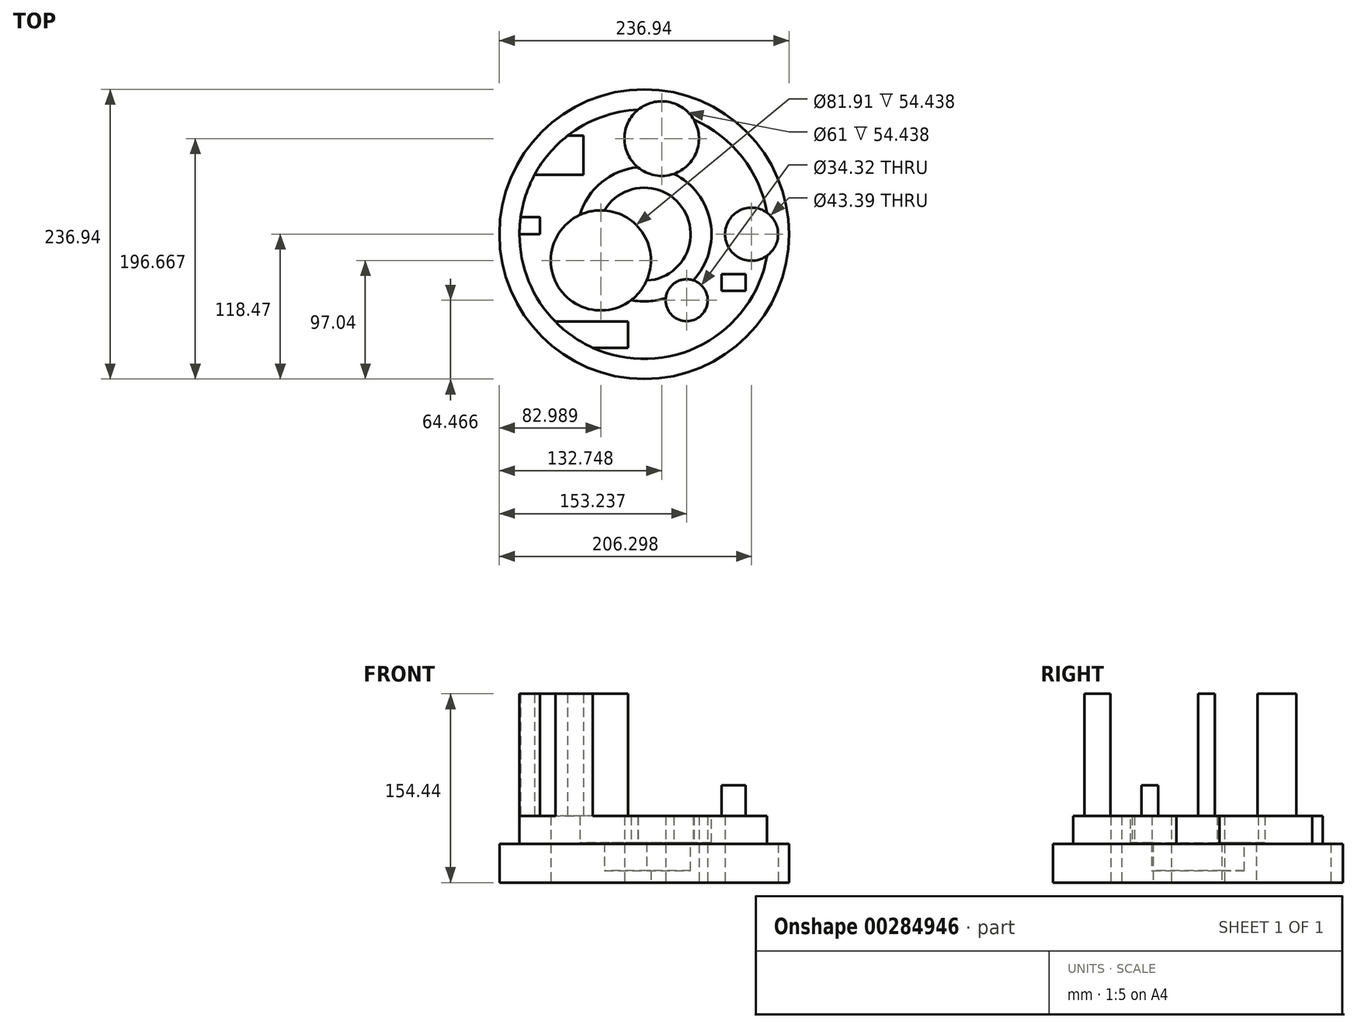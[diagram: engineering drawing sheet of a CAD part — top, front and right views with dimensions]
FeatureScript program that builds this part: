
annotation { "Feature Type Name" : "Feature", "Feature Type Description" : "" }
export const myFeature = defineFeature(function(context is Context, id is Id, definition is map)
    precondition{}
    {
        {
            var Q0;
            Q0=qCreatedBy(makeId("Front.planeOp"),FACE);
            var sketch = newSketch(context, id + "F0", { "sketchPlane" : qUnion([Q0])});
            skLineSegment(sketch, "E0", {"start": v(0, 0) * mm, "end": v(118.47, 0) * mm});
            skLineSegment(sketch, "E1", {"start": v(118.47, 0) * mm, "end": v(118.47, 31.74) * mm});
            skLineSegment(sketch, "E2", {"start": v(118.47, 31.74) * mm, "end": v(102.03, 31.74) * mm});
            skLineSegment(sketch, "E3", {"start": v(102.03, 31.74) * mm, "end": v(102.03, 54.44) * mm});
            skLineSegment(sketch, "E4", {"start": v(102.03, 54.44) * mm, "end": v(54.98, 54.44) * mm});
            skLineSegment(sketch, "E5", {"start": v(54.98, 54.44) * mm, "end": v(54.98, 32.6) * mm});
            skLineSegment(sketch, "E6", {"start": v(54.98, 32.6) * mm, "end": v(37.98, 32.6) * mm});
            skLineSegment(sketch, "E7", {"start": v(37.98, 32.6) * mm, "end": v(37.98, 9.63) * mm});
            skLineSegment(sketch, "E8", {"start": v(37.98, 9.63) * mm, "end": v(0, 9.63) * mm});
            skLineSegment(sketch, "E9", {"start": v(0, 9.63) * mm, "end": v(0, 0) * mm});
            skSolve(sketch);
        }
        {
            var Q0;
            Q0=makeQuery(id+"F0.imprint","IMPRINT",FACE,{"disambiguationData":[TD([[makeQuery(id+"F0.imprint","IMPRINT",EDGE,{"derivedFrom":sQuery(id+"F0.wireOp",EDGE,"E0")}),1.0]])]});
            var Q1;
            Q1=sQuery(id+"F0.wireOp",EDGE,"E9");
            revolve(context, id + "F1", {"entities" : qUnion([Q0]), "axis" : qUnion([Q1]), "revolveType" : RevolveType.FULL});
        }
        {
            var Q0;
            Q0=makeQuery(id+"F1.opRevolve","SWEPT_FACE",FACE,{"disambiguationData":[OSD([sQuery(id+"F0.wireOp",EDGE,"E0")])]});
            var sketch = newSketch(context, id + "F2", { "sketchPlane" : qUnion([Q0])});
            skCircle(sketch, "E10", {"center": v(87.83, 0) * mm, "radius": 21.7 * mm});
            skCircle(sketch, "E11", {"center": v(34.77, 54) * mm, "radius": 17.16 * mm});
            skCircle(sketch, "E12", {"center": v(-35.48, 21.43) * mm, "radius": 40.95 * mm});
            skCircle(sketch, "E13", {"center": v(14.28, -78.2) * mm, "radius": 30.5 * mm});
            skSolve(sketch);
        }
        {
            var Q0;
            Q0 = qSketchRegion(id + "F2", true);
            extrude(context, id + "F3", {"entities" : qUnion([Q0]), "operationType" : NewBodyOperationType.REMOVE, "oppositeDirection" : true, "depth" : 1000 * mm});
        }
        {
            var Q0;
            Q0=makeQuery(id+"F1.opRevolve","SWEPT_FACE",FACE,{"disambiguationData":[OSD([sQuery(id+"F0.wireOp",EDGE,"E4")])]});
            var sketch = newSketch(context, id + "F4", { "sketchPlane" : qUnion([Q0])});
            skLineSegment(sketch, "E14.bottom", {"start": v(-49.86, 80.53) * mm, "end": v(-89.68, 80.53) * mm});
            skLineSegment(sketch, "E14.top", {"start": v(-49.86, 48.65) * mm, "end": v(-89.68, 48.65) * mm});
            skLineSegment(sketch, "E14.left", {"start": v(-49.86, 80.53) * mm, "end": v(-49.86, 48.65) * mm});
            skLineSegment(sketch, "E14.right", {"start": v(-89.68, 80.53) * mm, "end": v(-89.68, 48.65) * mm});
            skLineSegment(sketch, "E15.bottom", {"start": v(-13.4, -71.58) * mm, "end": v(-83.96, -71.58) * mm});
            skLineSegment(sketch, "E15.top", {"start": v(-13.4, -92.9) * mm, "end": v(-83.96, -92.9) * mm});
            skLineSegment(sketch, "E15.left", {"start": v(-13.4, -71.58) * mm, "end": v(-13.4, -92.9) * mm});
            skLineSegment(sketch, "E15.right", {"start": v(-83.96, -71.58) * mm, "end": v(-83.96, -92.9) * mm});
            skLineSegment(sketch, "E16.bottom", {"start": v(-141.53, -1.14) * mm, "end": v(-161.53, -1.14) * mm});
            skLineSegment(sketch, "E16.top", {"start": v(-141.53, 28.86) * mm, "end": v(-161.53, 28.86) * mm});
            skLineSegment(sketch, "E16.left", {"start": v(-141.53, -1.14) * mm, "end": v(-141.53, 28.86) * mm});
            skLineSegment(sketch, "E16.right", {"start": v(-161.53, -1.14) * mm, "end": v(-161.53, 28.86) * mm});
            skLineSegment(sketch, "E17.bottom", {"start": v(-141.53, 13.86) * mm, "end": v(-85.38, 13.86) * mm});
            skLineSegment(sketch, "E17.top", {"start": v(-141.53, 0) * mm, "end": v(-85.38, 0) * mm});
            skLineSegment(sketch, "E17.left", {"start": v(-141.53, 13.86) * mm, "end": v(-141.53, 0) * mm});
            skLineSegment(sketch, "E17.right", {"start": v(-85.38, 13.86) * mm, "end": v(-85.38, 0) * mm});
            skSolve(sketch);
        }
        {
            var Q0;
            {var subQ4=sQuery(id+"F4.wireOp",EDGE,"E14.top");Q0=makeQuery(id+"F4.imprint","IMPRINT",FACE,{"disambiguationData":[TD([[makeQuery(id+"F4.imprint","IMPRINT",EDGE,{"derivedFrom":subQ4}),-1.0]])]});}
            var Q1;
            {var subQ0=sQuery(id+"F4.wireOp",EDGE,"E17.right");Q1=makeQuery(id+"F4.imprint","IMPRINT",FACE,{"disambiguationData":[TD([[makeQuery(id+"F4.imprint","IMPRINT",EDGE,{"derivedFrom":subQ0}),-1.0]])]});}
            var Q2;
            {var subQ0=sQuery(id+"F4.wireOp",EDGE,"E15.left");Q2=makeQuery(id+"F4.imprint","IMPRINT",FACE,{"disambiguationData":[TD([[makeQuery(id+"F4.imprint","IMPRINT",EDGE,{"derivedFrom":subQ0}),-1.0]])]});}
            extrude(context, id + "F5", {"entities" : qUnion([Q0, Q1, Q2]), "operationType" : NewBodyOperationType.ADD, "depth" : 100 * mm});
        }
        {
            var Q0;
            Q0=makeQuery(id+"F1.opRevolve","SWEPT_FACE",FACE,{"disambiguationData":[OSD([sQuery(id+"F0.wireOp",EDGE,"E4")])]});
            var sketch = newSketch(context, id + "F6", { "sketchPlane" : qUnion([Q0])});
            skLineSegment(sketch, "E18.bottom", {"start": v(82.95, -46.2) * mm, "end": v(63.25, -46.2) * mm});
            skLineSegment(sketch, "E18.top", {"start": v(82.95, -32.54) * mm, "end": v(63.25, -32.54) * mm});
            skLineSegment(sketch, "E18.left", {"start": v(82.95, -46.2) * mm, "end": v(82.95, -32.54) * mm});
            skLineSegment(sketch, "E18.right", {"start": v(63.25, -46.2) * mm, "end": v(63.25, -32.54) * mm});
            skSolve(sketch);
        }
        {
            var Q0;
            Q0 = qSketchRegion(id + "F6", true);
            extrude(context, id + "F7", {"entities" : qUnion([Q0]), "operationType" : NewBodyOperationType.ADD, "depth" : 25 * mm});
        }
    });
